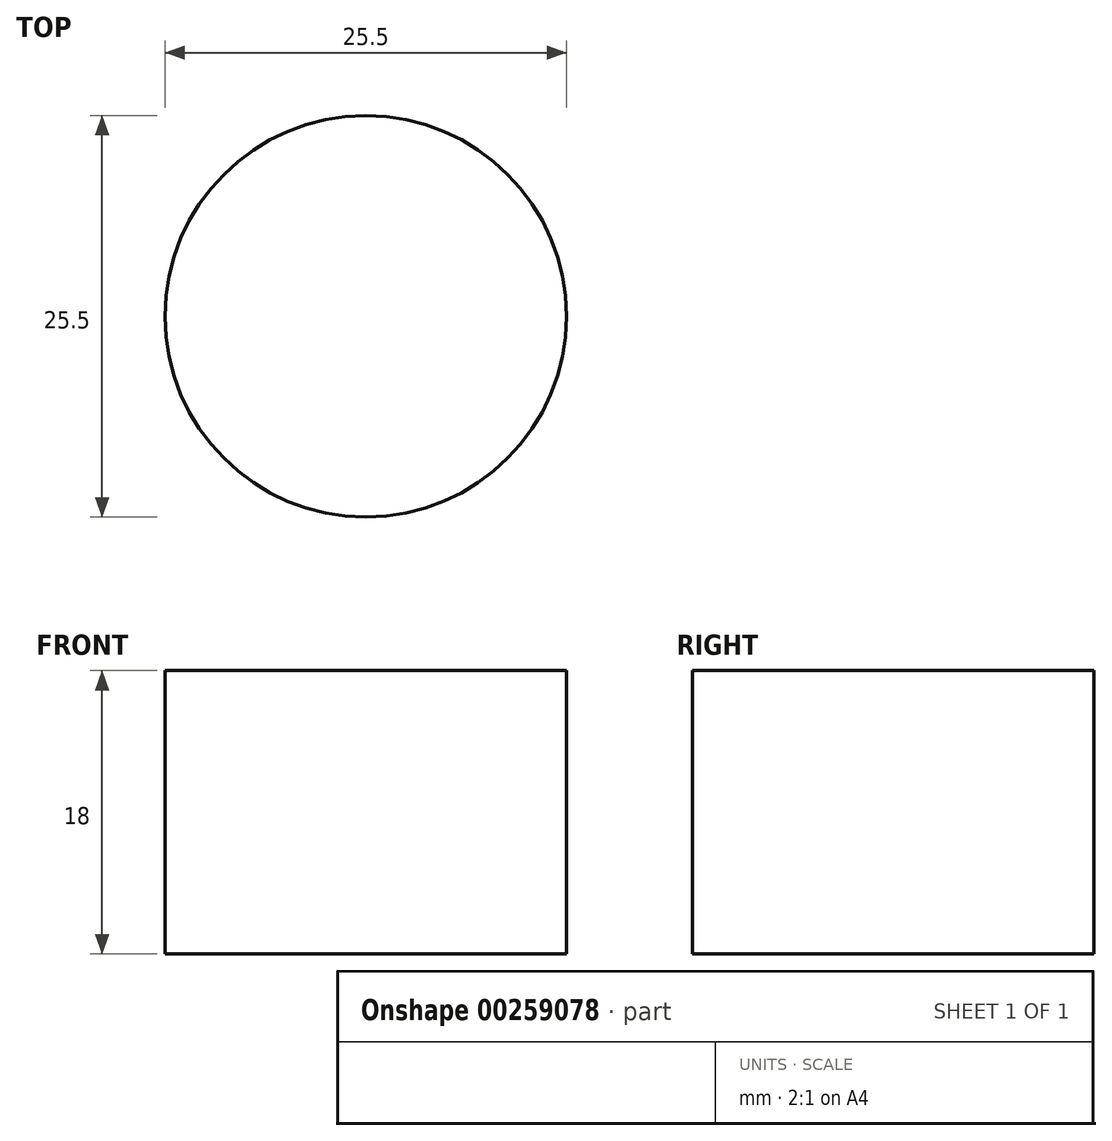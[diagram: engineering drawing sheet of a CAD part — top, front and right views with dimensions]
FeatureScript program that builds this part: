
annotation { "Feature Type Name" : "Feature", "Feature Type Description" : "" }
export const myFeature = defineFeature(function(context is Context, id is Id, definition is map)
    precondition{}
    {
        {
            var Q0;
            Q0=qCreatedBy(makeId("Top.planeOp"),FACE);
            var sketch = newSketch(context, id + "F0", { "sketchPlane" : qUnion([Q0])});
            skCircle(sketch, "E0", {"center": v(0, 0) * mm, "radius": 12.75 * mm});
            skSolve(sketch);
        }
        {
            var Q0;
            Q0 = qSketchRegion(id + "F0", true);
            extrude(context, id + "F1", {"entities" : qUnion([Q0]), "depth" : 18 * mm});
        }
    });
